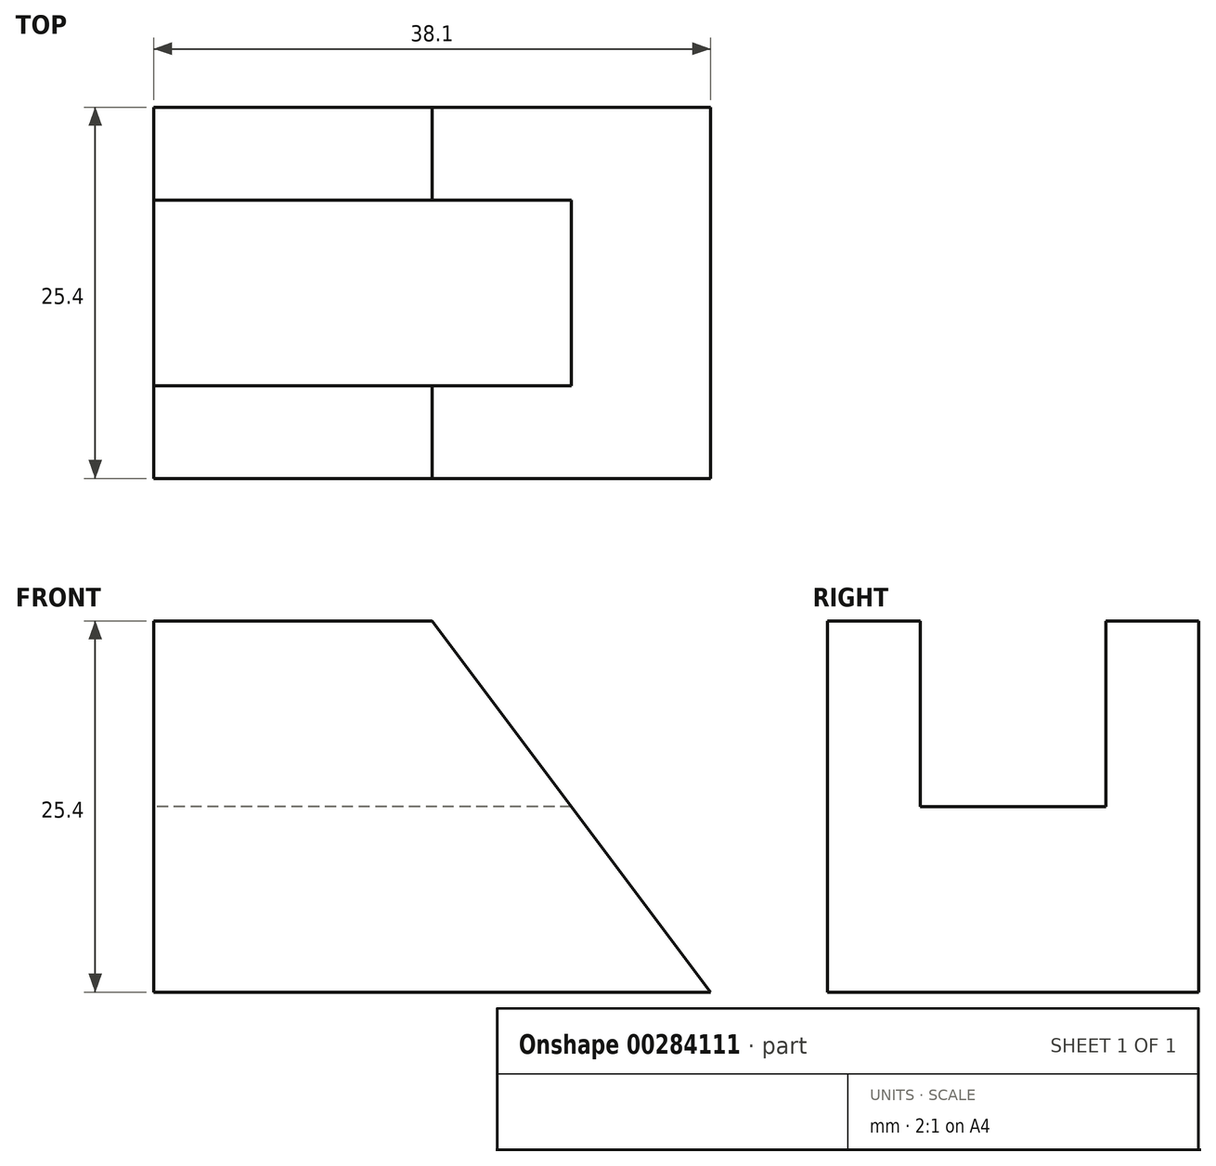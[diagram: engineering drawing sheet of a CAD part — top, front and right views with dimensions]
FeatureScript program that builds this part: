
annotation { "Feature Type Name" : "Feature", "Feature Type Description" : "" }
export const myFeature = defineFeature(function(context is Context, id is Id, definition is map)
    precondition{}
    {
        {
            var Q0;
            Q0=qCreatedBy(makeId("Front.planeOp"),FACE);
            var sketch = newSketch(context, id + "F0", { "sketchPlane" : qUnion([Q0])});
            skLineSegment(sketch, "E0", {"start": v(0, 0) * mm, "end": v(0, 25.4) * mm});
            skLineSegment(sketch, "E1", {"start": v(0, 25.4) * mm, "end": v(19.05, 25.4) * mm});
            skLineSegment(sketch, "E2", {"start": v(19.05, 25.4) * mm, "end": v(38.1, 0) * mm});
            skLineSegment(sketch, "E3", {"start": v(38.1, 0) * mm, "end": v(0, 0) * mm});
            skSolve(sketch);
        }
        {
            var Q0;
            Q0 = qSketchRegion(id + "F0", true);
            extrude(context, id + "F1", {"entities" : qUnion([Q0]), "endBound" : BoundingType.SYMMETRIC, "depth" : 25.4 * mm});
        }
        {
            var Q0;
            Q0=makeQuery(id+"F1.opExtrude","SWEPT_FACE",FACE,{"disambiguationData":[OSD([sQuery(id+"F0.wireOp",EDGE,"E0")])]});
            var sketch = newSketch(context, id + "F2", { "sketchPlane" : qUnion([Q0])});
            skLineSegment(sketch, "E4", {"start": v(-6.35, 25.4) * mm, "end": v(-6.35, 12.7) * mm});
            skLineSegment(sketch, "E5", {"start": v(-6.35, 12.7) * mm, "end": v(6.35, 12.7) * mm});
            skLineSegment(sketch, "E6", {"start": v(6.35, 12.7) * mm, "end": v(6.35, 25.4) * mm});
            skLineSegment(sketch, "E7", {"start": v(6.35, 25.4) * mm, "end": v(-6.35, 25.4) * mm});
            skLineSegment(sketch, "E8", {"start": v(0, 25.4) * mm, "end": v(0, 0) * mm, "construction": true});
            skSolve(sketch);
        }
        {
            var Q0;
            Q0 = qSketchRegion(id + "F2", true);
            extrude(context, id + "F3", {"entities" : qUnion([Q0]), "operationType" : NewBodyOperationType.REMOVE, "endBound" : BoundingType.THROUGH_ALL, "oppositeDirection" : true, "depth" : 25.4 * mm});
        }
    });
